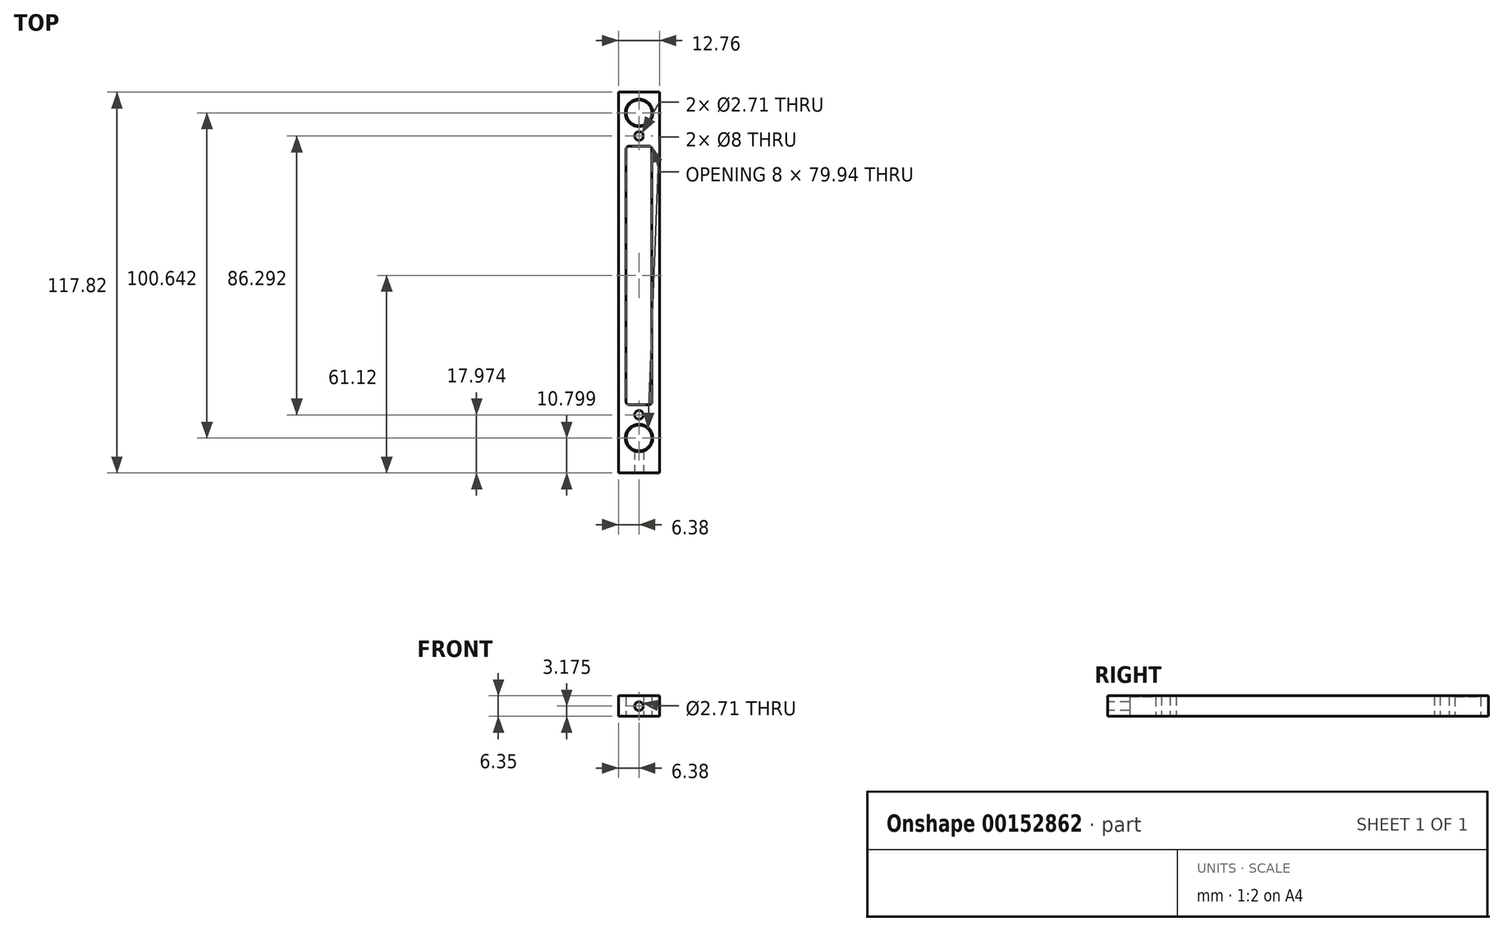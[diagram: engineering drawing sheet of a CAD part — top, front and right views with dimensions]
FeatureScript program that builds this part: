
annotation { "Feature Type Name" : "Feature", "Feature Type Description" : "" }
export const myFeature = defineFeature(function(context is Context, id is Id, definition is map)
    precondition{}
    {
        {
            var Q0;
            Q0=qCreatedBy(makeId("Top.planeOp"),FACE);
            var sketch = newSketch(context, id + "F0", { "sketchPlane" : qUnion([Q0])});
            skPoint(sketch, "E0.middle", {"position": v(0, 0) * mm});
            skLineSegment(sketch, "E1.bottom", {"start": v(4, -39.97) * mm, "end": v(-4, -39.97) * mm});
            skLineSegment(sketch, "E1.top", {"start": v(4, 39.97) * mm, "end": v(-4, 39.97) * mm});
            skLineSegment(sketch, "E1.left", {"start": v(4, -39.97) * mm, "end": v(4, 39.97) * mm});
            skLineSegment(sketch, "E1.right", {"start": v(-4, -39.97) * mm, "end": v(-4, 39.97) * mm});
            skLineSegment(sketch, "E2", {"start": v(0, 39.97) * mm, "end": v(0, 43.15) * mm, "construction": true});
            skLineSegment(sketch, "E3", {"start": v(0, 43.15) * mm, "end": v(0, 50.32) * mm, "construction": true});
            skLineSegment(sketch, "E4", {"start": v(0, 50.32) * mm, "end": v(0, 56.7) * mm, "construction": true});
            skCircle(sketch, "E5", {"center": v(0, 50.32) * mm, "radius": 4 * mm});
            skLineSegment(sketch, "E6", {"start": v(0, 50.32) * mm, "end": v(-6.38, 50.32) * mm, "construction": true});
            skCircle(sketch, "E7", {"center": v(0, 43.15) * mm, "radius": 3.18 * mm, "construction": true});
            skLineSegment(sketch, "E8", {"start": v(0, -61.12) * mm, "end": v(0, -50.32) * mm, "construction": true});
            skLineSegment(sketch, "E9", {"start": v(0, -50.32) * mm, "end": v(6.38, -50.32) * mm, "construction": true});
            skLineSegment(sketch, "E10", {"start": v(0, -50.32) * mm, "end": v(0, -43.15) * mm, "construction": true});
            skCircle(sketch, "E11", {"center": v(0, -50.32) * mm, "radius": 4 * mm});
            skCircle(sketch, "E12", {"center": v(0, -43.15) * mm, "radius": 1.35 * mm});
            skCircle(sketch, "E13", {"center": v(0, 43.15) * mm, "radius": 1.35 * mm});
            skLineSegment(sketch, "E14.bottom", {"start": v(-6.38, -61.12) * mm, "end": v(6.38, -61.12) * mm});
            skLineSegment(sketch, "E14.top", {"start": v(-6.38, 56.7) * mm, "end": v(6.38, 56.7) * mm});
            skLineSegment(sketch, "E14.left", {"start": v(-6.38, -61.12) * mm, "end": v(-6.38, 56.7) * mm});
            skLineSegment(sketch, "E14.right", {"start": v(6.38, -61.12) * mm, "end": v(6.38, 56.7) * mm});
            skSolve(sketch);
        }
        {
            var Q0;
            Q0=makeQuery(id+"F0.imprint","IMPRINT",FACE,{"disambiguationData":[TD([[makeQuery(id+"F0.imprint","IMPRINT",EDGE,{"derivedFrom":sQuery(id+"F0.wireOp",EDGE,"E0.bottom")}),-1.0]])]});
            var Q1;
            Q1=makeQuery(id+"F0.imprint","IMPRINT",FACE,{"disambiguationData":[TD([[makeQuery(id+"F0.imprint","IMPRINT",EDGE,{"derivedFrom":sQuery(id+"F0.wireOp",EDGE,"E1.bottom")}),1.0]])]});
            extrude(context, id + "F1", {"entities" : qUnion([Q0, Q1]), "depth" : 6.35 * mm});
        }
        {
            var Q0;
            Q0=makeQuery(id+"F1.opExtrude","SWEPT_EDGE",EDGE,{"disambiguationData":[OSD([sQuery(id+"F0.wireOp",EDGE,"E1.bottom"),sQuery(id+"F0.wireOp",EDGE,"E1.left")])]});
            var Q1;
            Q1=makeQuery(id+"F1.opExtrude","SWEPT_EDGE",EDGE,{"disambiguationData":[OSD([sQuery(id+"F0.wireOp",EDGE,"E1.bottom"),sQuery(id+"F0.wireOp",EDGE,"E1.right")])]});
            var Q2;
            Q2=makeQuery(id+"F1.opExtrude","SWEPT_EDGE",EDGE,{"disambiguationData":[OSD([sQuery(id+"F0.wireOp",EDGE,"E1.top"),sQuery(id+"F0.wireOp",EDGE,"E1.right")])]});
            var Q3;
            Q3=makeQuery(id+"F1.opExtrude","SWEPT_EDGE",EDGE,{"disambiguationData":[OSD([sQuery(id+"F0.wireOp",EDGE,"E1.top"),sQuery(id+"F0.wireOp",EDGE,"E1.left")])]});
            fillet(context, id + "F2", {"entities" : qUnion([Q0, Q1, Q2, Q3]), "radius" : 0.8 * mm, "tangentPropagation" : true, "allowEdgeOverflow" : false});
        }
        {
            var Q0;
            Q0=makeQuery(id+"F1.opExtrude","CAP_EDGE",EDGE,{"disambiguationData":[OSD([sQuery(id+"F0.wireOp",EDGE,"E5")])],"isStart":false});
            var Q1;
            Q1=makeQuery(id+"F1.opExtrude","CAP_EDGE",EDGE,{"disambiguationData":[OSD([sQuery(id+"F0.wireOp",EDGE,"E11")])],"isStart":false});
            chamfer(context, id + "F3", {"entities" : qUnion([Q0, Q1]), "width" : 0.25 * mm, "tangentPropagation" : true});
        }
        {
            var Q0;
            Q0=makeQuery(id+"F1.opExtrude","SWEPT_FACE",FACE,{"disambiguationData":[OSD([sQuery(id+"F0.wireOp",EDGE,"E14.bottom")])]});
            var sketch = newSketch(context, id + "F4", { "sketchPlane" : qUnion([Q0])});
            skLineSegment(sketch, "E15", {"start": v(0, 6.35) * mm, "end": v(0, 0) * mm, "construction": true});
            skCircle(sketch, "E16", {"center": v(0, 3.18) * mm, "radius": 1.35 * mm});
            skSolve(sketch);
        }
        {
            var Q0;
            Q0 = qSketchRegion(id + "F4", true);
            var Q1;
            Q1=makeQuery(id+"F1.opExtrude","SWEPT_FACE",FACE,{"disambiguationData":[OSD([sQuery(id+"F0.wireOp",EDGE,"E11")])]});
            extrude(context, id + "F5", {"entities" : qUnion([Q0]), "operationType" : NewBodyOperationType.REMOVE, "endBound" : BoundingType.UP_TO_SURFACE, "oppositeDirection" : true, "endBoundEntityFace" : qUnion([Q1]), "depth" : 25.4 * mm});
        }
    });
